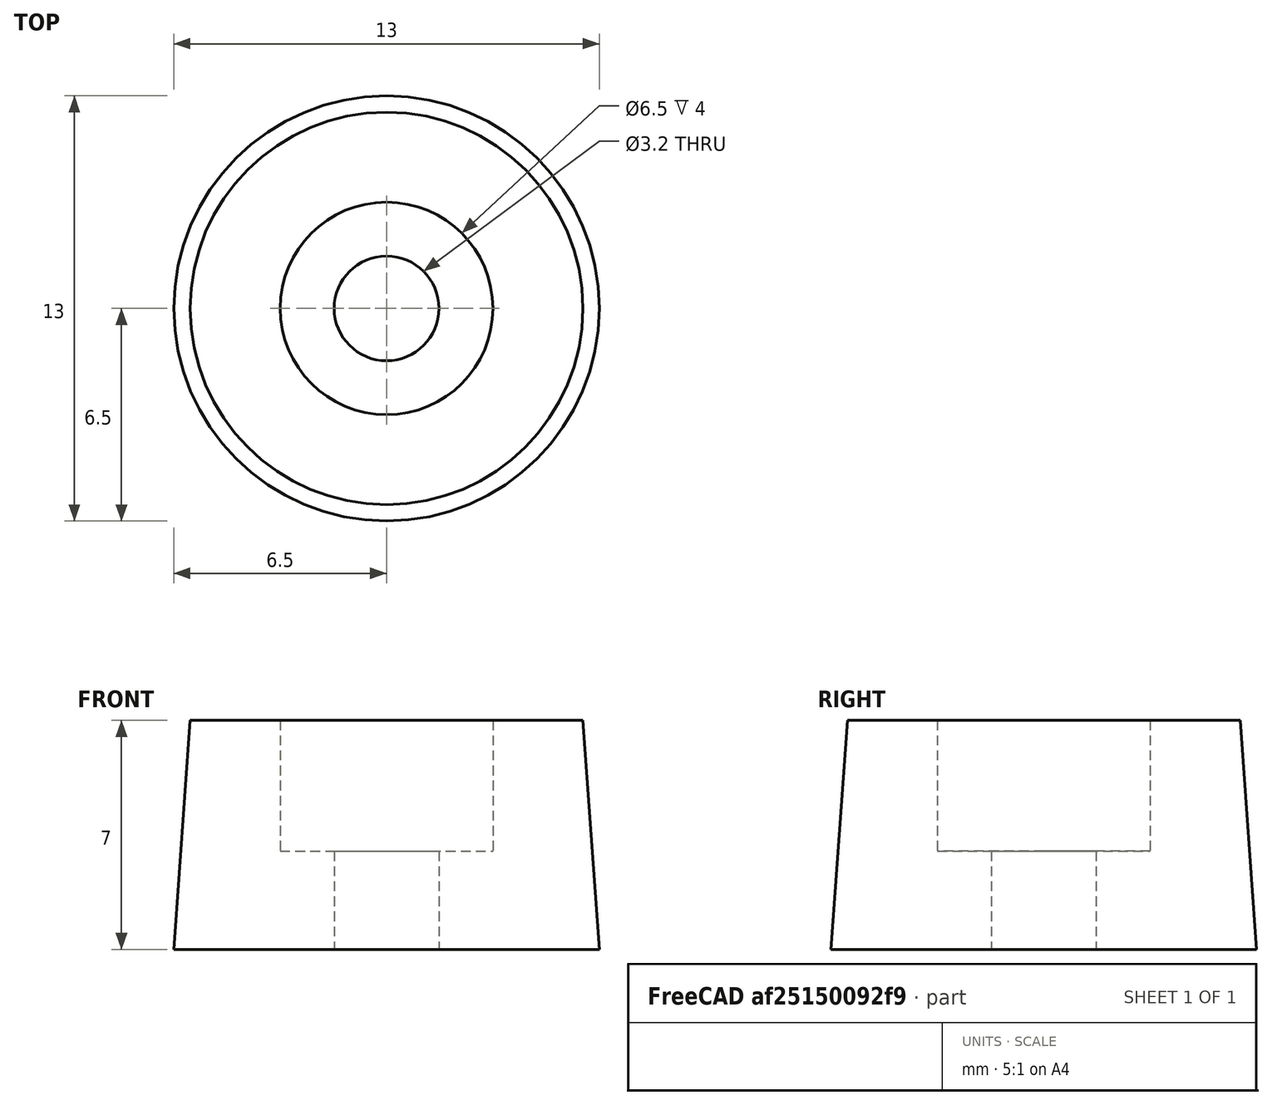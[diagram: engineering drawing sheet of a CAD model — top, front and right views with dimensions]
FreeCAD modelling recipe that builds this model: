
FCSTD DOCUMENT  (FreeCAD 0.16R5861 (Git))
Label: flexy_bed_foot_v0.1
License: All rights reserved
LicenseURL: http://en.wikipedia.org/wiki/All_rights_reserved
objects: Sketcher::SketchObject×1, PartDesign::Revolution×1
note: 3 computed .brp shape members not serialized (recipe doc carries the construction recipe); baked Part::Feature solids carry a one-line shape summary decoded from their .brp

FEATURE [Sketcher::SketchObject] Sketch
  Placement = pos=(0,0,0) rot=(-1,0,0;4.71239rad)
  sketch-geometry (6):
    g0: LineSegment StartX=-1.6 StartY=0 StartZ=0 EndX=-6.5 EndY=0 EndZ=0
    g1: LineSegment StartX=-6.5 StartY=0 StartZ=0 EndX=-6 EndY=7 EndZ=0
    g2: LineSegment StartX=-6 StartY=7 StartZ=0 EndX=-3.25 EndY=7 EndZ=0
    g3: LineSegment StartX=-3.25 StartY=7 StartZ=0 EndX=-3.25 EndY=3 EndZ=0
    g4: LineSegment StartX=-3.25 StartY=3 StartZ=0 EndX=-1.6 EndY=3 EndZ=0
    g5: LineSegment StartX=-1.6 StartY=3 StartZ=0 EndX=-1.6 EndY=0 EndZ=0
  constraints (18):
    c: PointOnObject(g0,g-1)
    c: PointOnObject(g0,g-1)
    c: Coincident(g0,g1)
    c: Coincident(g1,g2)
    c: Horizontal(g2)
    c: Coincident(g2,g3)
    c: Vertical(g3)
    c: Coincident(g3,g4)
    c: Horizontal(g4)
    c: Coincident(g4,g5)
    c: Coincident(g5,g0)
    c: Vertical(g5)
    c: DistanceX(g-1,g0) = -6.5
    c: DistanceX(g-1,g0) = -1.6
    c: DistanceX(g-1,g3) = -3.25
    c: DistanceY(g-1,g2) = 7
    c: DistanceX(g1,g0) = -0.5
    c: DistanceY(g5) = -3
FEATURE [PartDesign::Revolution] Revolution
  Angle = 360
  Axis = (0,0,1)
  Base = (0,0,0)
  Placement = pos=(0,0,0) rot=(-1,0,0;4.71239rad)
  ReferenceAxis = -> Sketch [V_Axis]
  Sketch = -> Sketch
